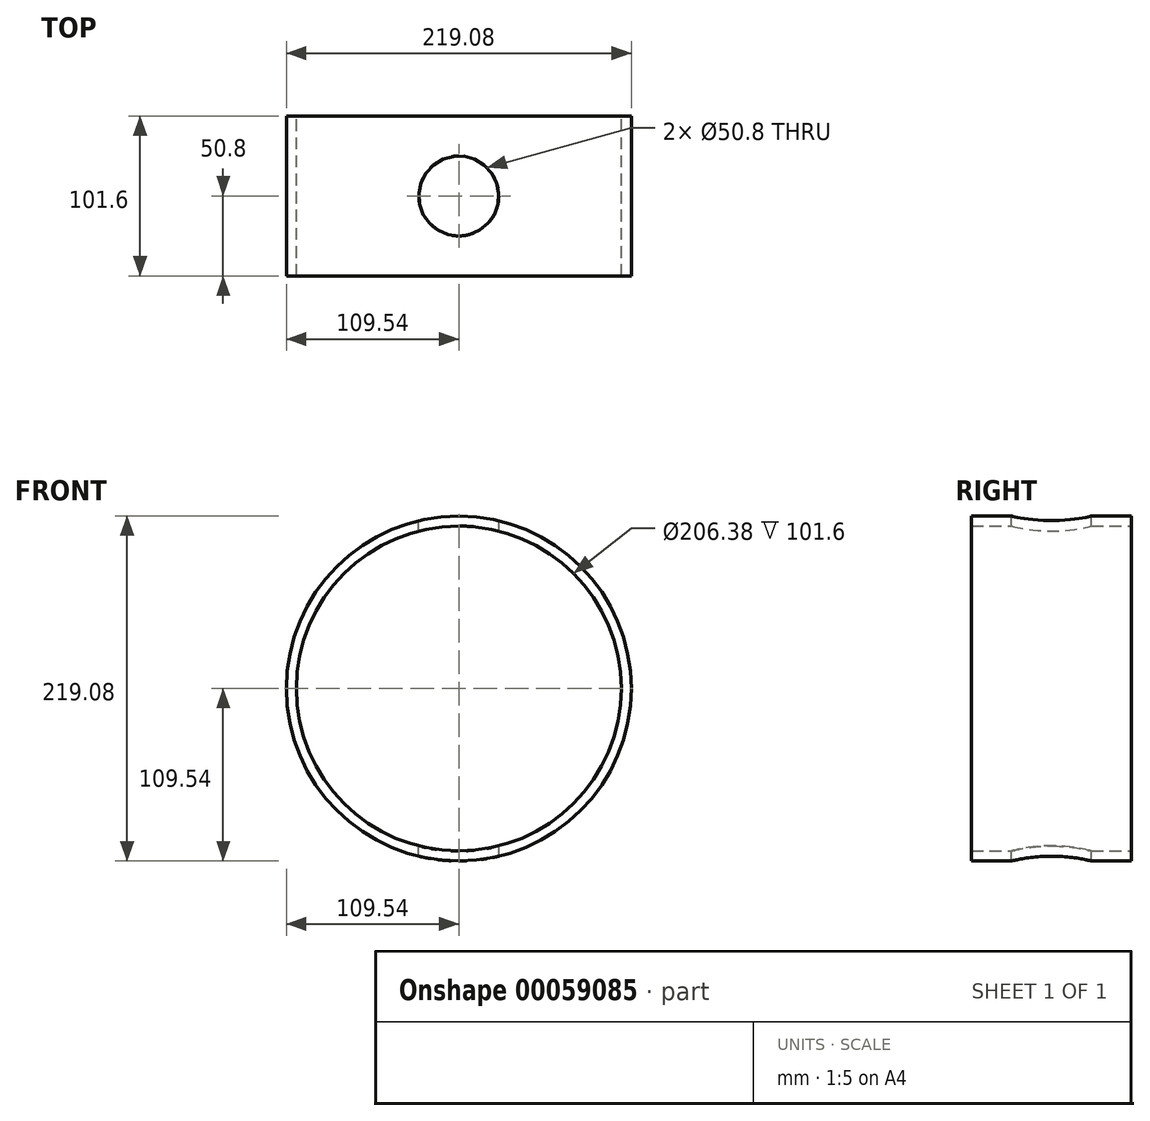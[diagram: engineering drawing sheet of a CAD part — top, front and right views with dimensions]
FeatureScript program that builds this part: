
annotation { "Feature Type Name" : "Feature", "Feature Type Description" : "" }
export const myFeature = defineFeature(function(context is Context, id is Id, definition is map)
    precondition{}
    {
        {
            var Q0;
            Q0=qCreatedBy(makeId("Front.planeOp"),FACE);
            var sketch = newSketch(context, id + "F0", { "sketchPlane" : qUnion([Q0])});
            skCircle(sketch, "E0", {"center": v(0, 0) * mm, "radius": 109.54 * mm});
            skCircle(sketch, "E1.0", {"center": v(0, 0) * mm, "radius": 103.19 * mm});
            skSolve(sketch);
        }
        {
            var Q0;
            Q0 = qSketchRegion(id + "F0", true);
            var Q1;
            Q1 = qSketchRegion(id + "F2", true);
            extrude(context, id + "F1", {"entities" : qUnion([Q0, Q1]), "depth" : 50.8 * mm, "hasSecondDirection" : true, "secondDirectionOppositeDirection" : true, "secondDirectionDepth" : 50.8 * mm});
        }
        {
            var Q0;
            Q0=qCreatedBy(makeId("Top.planeOp"),FACE);
            var sketch = newSketch(context, id + "F2", { "sketchPlane" : qUnion([Q0])});
            skSolve(sketch);
        }
        {
            var Q0;
            Q0=qCreatedBy(makeId("Top.planeOp"),FACE);
            var sketch = newSketch(context, id + "F3", { "sketchPlane" : qUnion([Q0])});
            skCircle(sketch, "E2", {"center": v(0, 0) * mm, "radius": 25.4 * mm});
            skSolve(sketch);
        }
        {
            var Q0;
            Q0 = qSketchRegion(id + "F3", true);
            extrude(context, id + "F4", {"entities" : qUnion([Q0]), "operationType" : NewBodyOperationType.REMOVE, "endBound" : BoundingType.THROUGH_ALL, "oppositeDirection" : true, "depth" : 25.4 * mm, "hasSecondDirection" : true, "secondDirectionBound" : SecondDirectionBoundingType.THROUGH_ALL, "secondDirectionOppositeDirection" : false, "secondDirectionDepth" : 25.4 * mm});
        }
    });
